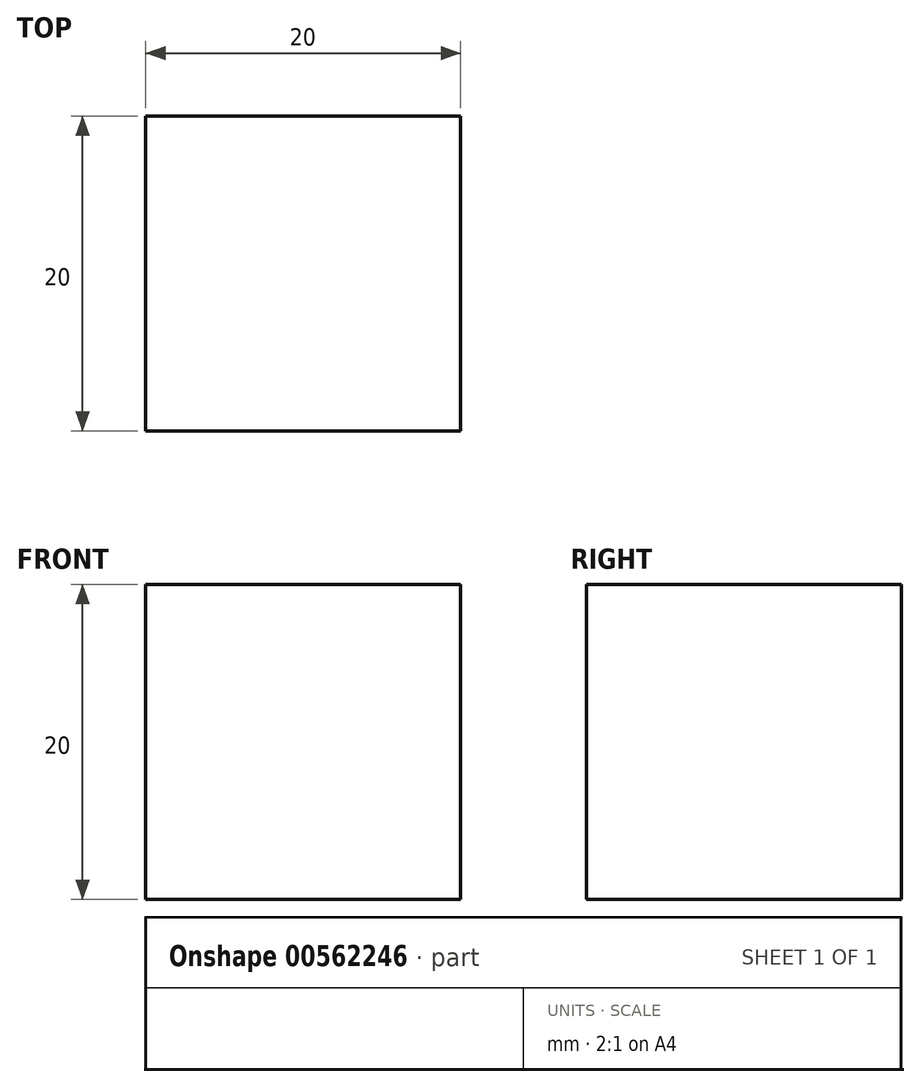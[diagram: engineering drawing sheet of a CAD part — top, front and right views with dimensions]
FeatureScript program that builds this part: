
annotation { "Feature Type Name" : "Feature", "Feature Type Description" : "" }
export const myFeature = defineFeature(function(context is Context, id is Id, definition is map)
    precondition{}
    {
        {
            var Q0;
            Q0=qCreatedBy(makeId("Top.planeOp"),FACE);
            var sketch = newSketch(context, id + "F0", { "sketchPlane" : qUnion([Q0])});
            skLineSegment(sketch, "E0.bottom", {"start": v(10, 10) * mm, "end": v(-10, 10) * mm});
            skLineSegment(sketch, "E0.top", {"start": v(10, -10) * mm, "end": v(-10, -10) * mm});
            skLineSegment(sketch, "E0.left", {"start": v(10, 10) * mm, "end": v(10, -10) * mm});
            skLineSegment(sketch, "E0.right", {"start": v(-10, 10) * mm, "end": v(-10, -10) * mm});
            skPoint(sketch, "E0.middle", {"position": v(0, 0) * mm});
            skSolve(sketch);
        }
        {
            var Q0;
            Q0 = qSketchRegion(id + "F0", true);
            extrude(context, id + "F1", {"entities" : qUnion([Q0]), "depth" : 20 * mm, "offsetDistance" : 25 * mm});
        }
    });
